# Revit family: FP_Revit_18_CDV3-365H-N_Cooktop_90001918A
name_source: partatom
category: Specialty Equipment
revit_build: Autodesk Revit 2018 (Build: 20170223_1515(x64)
units: mm (PartAtom-declared; Revit-internal decimal feet)

## family parameters
Always vertical = Yes
Cut with Voids When Loaded = Yes
OmniClass Number = 23.40.40.14.17.11
OmniClass Title = Cookers, Ovens, Stoves
Part Type = Normal
Room Calculation Point = No
Round Connector Dimension = Use Diameter
Shared = No
Work Plane-Based = No

## types (4) — shared parameters
Cavity - Depth = 502 mm  [stored 1.64698 ft]
Cavity - Height = 112 mm  [stored 0.367454 ft]
Cavity - Width = 883 mm  [stored 2.89698 ft]
Chassis - Depth = 497 mm
Chassis - Height = 102 mm
Chassis - Width = 874 mm  [stored 2.86745 ft]
Clearance - Below Combustible = 65 mm  [stored 0.213255 ft]
Clearance - Below Non-Combustible = 70 mm  [stored 0.229659 ft]
Clearance - Overhead Combustible = 914 mm  [stored 2.99869 ft]
Clearance - Overhead Non-Combustible = 762 mm  [stored 2.5 ft]
Clearance - Overhead Rangehood = 914 mm  [stored 2.99869 ft]
Clearance - Rear Combustible = 51 mm
Clearance - Side Combustible = 305 mm  [stored 1.00066 ft]
Connector Note - Electrical = 120 V, 0.1 A Max, 60 Hz
Description = 36" Professional Gas Cooktop,
Manufacturer = Fisher & Paykel Appliances
Material - Body = Fisher & Paykel - Grey
Material - Burners & Trivets = Fisher & Paykel - Black, Matte
Material - Cooktop = Fisher & Paykel - Stainless Steel
Material - Trim = Fisher & Paykel - Aluminium, Dark
Product - Depth = 533 mm
Product - Height = 162 mm  [stored 0.531496 ft]
Product - Width = 915 mm  [stored 3.00197 ft]
URL = www.fisherpaykel.com
Visibility - Clearance Required = Yes

## per-type parameters (varying)
| type | Connector Note - Gas | Model | Visibility - Gas Elbow Rear Facing | Visibility - Gas Elbow Side Facing |
| CDV3-365H-L | LP Supply Pressure = 11" to 14" WC, 1/2" NPT Minimum 5/8" dia. flex line | CDV3-365H-L | Yes | Yes |
| CDV3-365H-N | NG Supply Pressure = 6" to 9" WC, 1/2" NPT Minimum 5/8" dia. flex line | CDV3-365H-N | No | No |
| CDV3-365-N | NG Supply Pressure = 6" to 9" WC, 1/2" NPT Minimum 5/8" dia. flex line | CDV3-365H-N | Yes | Yes |
| CDV3-365-L | LP Supply Pressure = 11" to 14" WC, 1/2" NPT Minimum 5/8" dia. flex line | CDV3-365-L | Yes | Yes |

note: [stored X ft] marks values corroborated as IEEE doubles in the binary element streams (Revit-internal decimal feet)

## geometry (parser evidence)
native form markers: Sweep x17
no freeform markers — native parametric forms only
